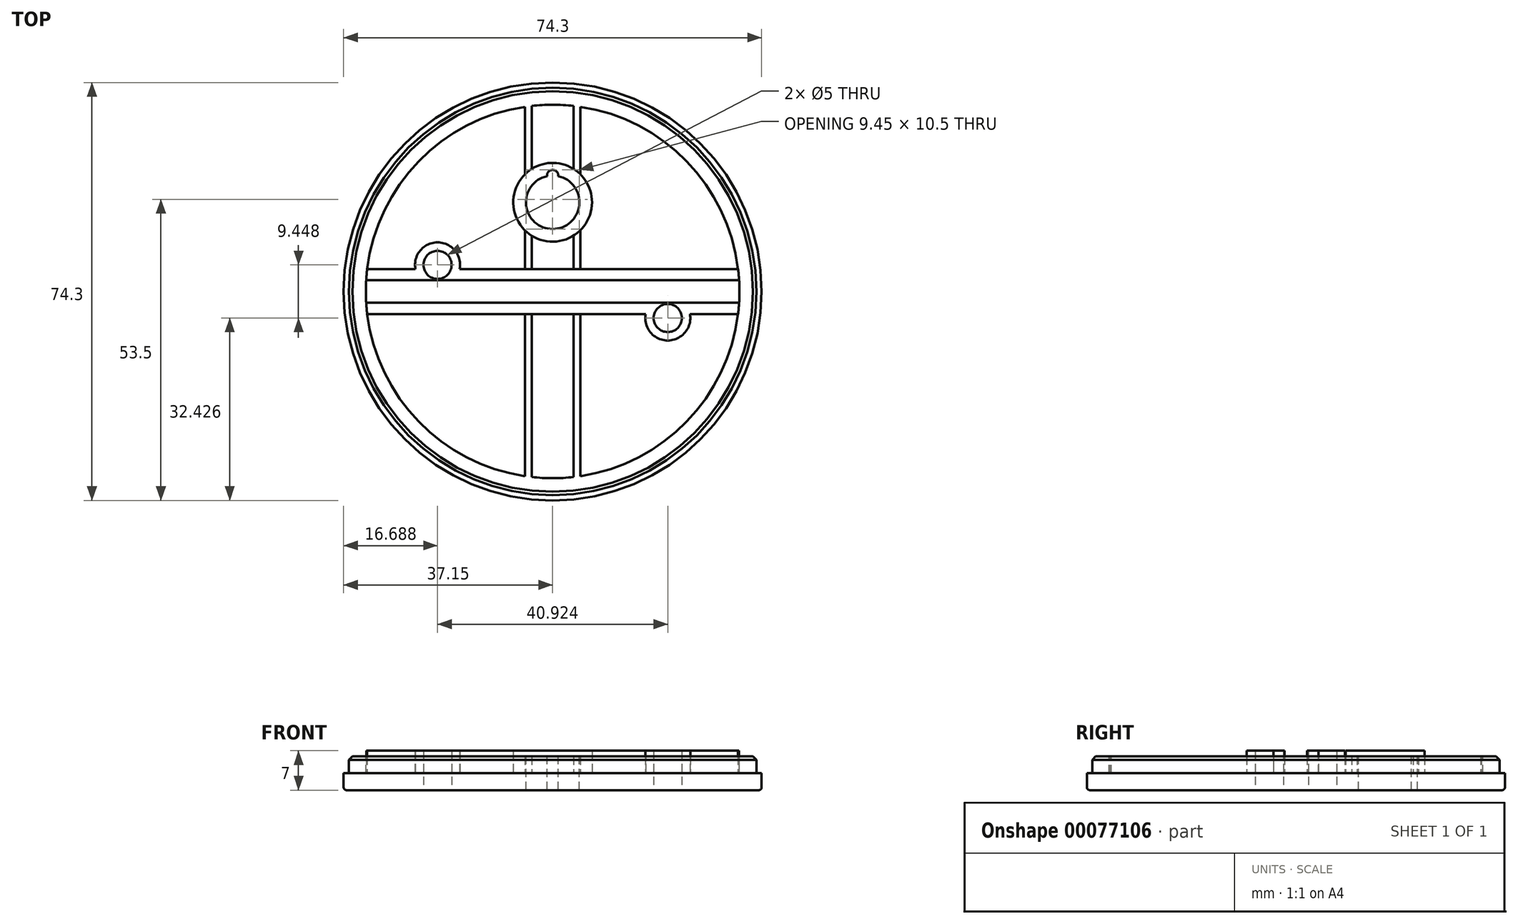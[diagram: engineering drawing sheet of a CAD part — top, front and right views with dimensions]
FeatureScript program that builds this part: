
annotation { "Feature Type Name" : "Feature", "Feature Type Description" : "" }
export const myFeature = defineFeature(function(context is Context, id is Id, definition is map)
    precondition{}
    {
        {
            var Q0;
            Q0=qCreatedBy(makeId("Front.planeOp"),FACE);
            var sketch = newSketch(context, id + "F0", { "sketchPlane" : qUnion([Q0])});
            skLineSegment(sketch, "E0.bottom", {"start": v(0, 0) * mm, "end": v(-33.2, 0) * mm});
            skLineSegment(sketch, "E0.top", {"start": v(0, -3) * mm, "end": v(-37.15, -3) * mm});
            skLineSegment(sketch, "E0.left", {"start": v(0, 0) * mm, "end": v(0, -3) * mm});
            skLineSegment(sketch, "E0.right", {"start": v(-37.15, 0) * mm, "end": v(-37.15, -3) * mm});
            skLineSegment(sketch, "E1.top", {"start": v(-36.2, 3) * mm, "end": v(-33.2, 3) * mm});
            skLineSegment(sketch, "E1.left", {"start": v(-36.2, 0) * mm, "end": v(-36.2, 3) * mm});
            skLineSegment(sketch, "E1.right", {"start": v(-33.2, 0) * mm, "end": v(-33.2, 3) * mm});
            skLineSegment(sketch, "E2.trimOffspring", {"start": v(-36.2, 0) * mm, "end": v(-37.15, 0) * mm});
            skLineSegment(sketch, "E3", {"start": v(0, 23.02) * mm, "end": v(0, -39) * mm, "construction": true});
            skSolve(sketch);
        }
        {
            var Q0;
            Q0=makeQuery(id+"F0.imprint","IMPRINT",FACE,{"disambiguationData":[TD([[makeQuery(id+"F0.imprint","IMPRINT",EDGE,{"derivedFrom":sQuery(id+"F0.wireOp",EDGE,"E0.bottom")}),1.0]])]});
            var Q1;
            Q1=sQuery(id+"F0.wireOp",EDGE,"E3");
            revolve(context, id + "F1", {"surfaceOperationType" : NewSurfaceOperationType.NEW, "entities" : qUnion([Q0]), "axis" : qUnion([Q1]), "revolveType" : RevolveType.FULL});
        }
        {
            var Q0;
            Q0=makeQuery(id+"F1.opRevolve","SWEPT_FACE",FACE,{"disambiguationData":[OSD([sQuery(id+"F0.wireOp",EDGE,"E0.bottom")])]});
            var sketch = newSketch(context, id + "F2", { "sketchPlane" : qUnion([Q0])});
            skLineSegment(sketch, "E4.bottom", {"start": v(-34.3, 2) * mm, "end": v(34, 2) * mm});
            skLineSegment(sketch, "E4.top", {"start": v(-34.3, 4) * mm, "end": v(34, 4) * mm});
            skLineSegment(sketch, "E4.left", {"start": v(-34.3, 2) * mm, "end": v(-34.3, 4) * mm});
            skLineSegment(sketch, "E4.right", {"start": v(34, 2) * mm, "end": v(34, 4) * mm});
            skLineSegment(sketch, "E5.MirrorCS", {"start": v(-34.3, -2) * mm, "end": v(34, -2) * mm});
            skLineSegment(sketch, "E6.MirrorCS", {"start": v(-34.3, -2) * mm, "end": v(-34.3, -4) * mm});
            skLineSegment(sketch, "E7.MirrorCS", {"start": v(-34.3, -4) * mm, "end": v(34, -4) * mm});
            skLineSegment(sketch, "E8.MirrorCS", {"start": v(34, -2) * mm, "end": v(34, -4) * mm});
            skSolve(sketch);
        }
        {
            var Q0;
            {var subQ0=sQuery(id+"F2.wireOp",EDGE,"E4.bottom");var subQ1=makeQuery(id+"F1.opRevolve","SWEPT_EDGE",EDGE,{"disambiguationData":[OSD([sQuery(id+"F0.wireOp",EDGE,"E0.bottom"),sQuery(id+"F0.wireOp",EDGE,"E1.right")])]});var subQ2=makeQuery(id+"F2.imprint","INTERSECT",VERTEX,{"disambiguationData":[OD(0.0)],"derivedFrom":[subQ1,subQ0]});Q0=makeQuery(id+"F2.imprint","IMPRINT",FACE,{"disambiguationData":[TD([[makeQuery(id+"F2.imprint","IMPRINT",EDGE,{"disambiguationData":[TD([[subQ2,-1.0]])],"derivedFrom":subQ0}),1.0]])]});}
            var Q1;
            {var subQ0=sQuery(id+"F2.wireOp",EDGE,"E5.MirrorCS");var subQ1=makeQuery(id+"F1.opRevolve","SWEPT_EDGE",EDGE,{"disambiguationData":[OSD([sQuery(id+"F0.wireOp",EDGE,"E0.bottom"),sQuery(id+"F0.wireOp",EDGE,"E1.right")])]});var subQ2=makeQuery(id+"F2.imprint","INTERSECT",VERTEX,{"disambiguationData":[OD(0.0)],"derivedFrom":[subQ1,subQ0]});Q1=makeQuery(id+"F2.imprint","IMPRINT",FACE,{"disambiguationData":[TD([[makeQuery(id+"F2.imprint","IMPRINT",EDGE,{"disambiguationData":[TD([[subQ2,-1.0]])],"derivedFrom":subQ0}),-1.0]])]});}
            extrude(context, id + "F3", {"entities" : qUnion([Q0, Q1]), "operationType" : NewBodyOperationType.ADD, "depth" : 4 * mm, "offsetDistance" : 25 * mm});
        }
        {
            var Q0;
            Q0=makeQuery(id+"F3.boolean.opBoolean","SPLIT",FACE,{"disambiguationData":[TD([makeQuery(id+"F3.opExtrude","SWEPT_FACE",FACE,{"disambiguationData":[OSD([sQuery(id+"F2.wireOp",EDGE,"E4.top")])]})])],"derivedFrom":makeQuery(id+"F1.opRevolve","SWEPT_FACE",FACE,{"disambiguationData":[OSD([sQuery(id+"F0.wireOp",EDGE,"E0.bottom")])]})});
            var sketch = newSketch(context, id + "F4", { "sketchPlane" : qUnion([Q0])});
            skCircle(sketch, "E9", {"center": v(0, 0) * mm, "radius": 25 * mm});
            skSolve(sketch);
        }
        {
            var Q0;
            {var subQ0=sQuery(id+"F4.wireOp",EDGE,"E9");var subQ1=sQuery(id+"F2.wireOp",EDGE,"E4.top");var subQ2=makeQuery(id+"F3.opExtrude","CAP_EDGE",EDGE,{"disambiguationData":[OSD([subQ1])],"isStart":true});var subQ3=makeQuery(id+"F4.imprint","INTERSECT",VERTEX,{"disambiguationData":[OD(0.0)],"derivedFrom":[subQ2,subQ0]});Q0=makeQuery(id+"F4.imprint","IMPRINT",FACE,{"disambiguationData":[TD([[makeQuery(id+"F4.imprint","IMPRINT",EDGE,{"disambiguationData":[TD([[subQ3,1.0]])],"derivedFrom":subQ0}),-1.0]])]});}
            var sketch = newSketch(context, id + "F5", { "sketchPlane" : qUnion([Q0])});
            skLineSegment(sketch, "E10", {"start": v(-33.33, 7.7) * mm, "end": v(0, 0) * mm, "construction": true});
            skLineSegment(sketch, "E11", {"start": v(0, 0) * mm, "end": v(33.42, -7.72) * mm, "construction": true});
            skLineSegment(sketch, "E12.bottom", {"start": v(-4.93, 3.16) * mm, "end": v(-3.73, 3.16) * mm});
            skLineSegment(sketch, "E12.top", {"start": v(-4.93, 33.8) * mm, "end": v(-3.73, 33.8) * mm});
            skLineSegment(sketch, "E12.left", {"start": v(-4.93, 3.16) * mm, "end": v(-4.93, 33.8) * mm});
            skLineSegment(sketch, "E12.right", {"start": v(-3.73, 3.16) * mm, "end": v(-3.73, 33.8) * mm});
            skLineSegment(sketch, "E13.MirrorCS", {"start": v(3.73, 3.16) * mm, "end": v(3.73, 33.8) * mm});
            skLineSegment(sketch, "E14.MirrorCS", {"start": v(4.93, 3.16) * mm, "end": v(4.93, 33.8) * mm});
            skLineSegment(sketch, "E15.MirrorCS", {"start": v(4.93, 33.8) * mm, "end": v(3.73, 33.8) * mm});
            skLineSegment(sketch, "E16.MirrorCS", {"start": v(4.93, 3.16) * mm, "end": v(3.73, 3.16) * mm});
            skLineSegment(sketch, "E17.MirrorCS", {"start": v(-4.93, -33.8) * mm, "end": v(-3.73, -33.8) * mm});
            skLineSegment(sketch, "E18.MirrorCS", {"start": v(-3.73, -3.16) * mm, "end": v(-3.73, -33.8) * mm});
            skLineSegment(sketch, "E19.MirrorCS", {"start": v(-4.93, -3.16) * mm, "end": v(-3.73, -3.16) * mm});
            skLineSegment(sketch, "E20.MirrorCS", {"start": v(-4.93, -3.16) * mm, "end": v(-4.93, -33.8) * mm});
            skLineSegment(sketch, "E21.MirrorCS", {"start": v(4.93, -3.16) * mm, "end": v(3.73, -3.16) * mm});
            skLineSegment(sketch, "E22.MirrorCS", {"start": v(4.93, -33.8) * mm, "end": v(3.73, -33.8) * mm});
            skLineSegment(sketch, "E23.MirrorCS", {"start": v(3.73, -3.16) * mm, "end": v(3.73, -33.8) * mm});
            skLineSegment(sketch, "E24.MirrorCS", {"start": v(4.93, -3.16) * mm, "end": v(4.93, -33.8) * mm});
            skCircle(sketch, "E25", {"center": v(0, 0) * mm, "radius": 21 * mm, "construction": true});
            skCircle(sketch, "E26", {"center": v(-20.46, 4.72) * mm, "radius": 2.5 * mm});
            skCircle(sketch, "E27", {"center": v(20.46, -4.72) * mm, "radius": 2.5 * mm});
            skArc(sketch, "E28", {"start": v(-17.49, 2.05) * mm, "mid": v(-20.46, 8.72) * mm, "end": v(-23.44, 2.05) * mm});
            skArc(sketch, "E29", {"start": v(17.54, -2) * mm, "mid": v(20.46, -8.72) * mm, "end": v(23.38, -2) * mm});
            skLineSegment(sketch, "E30", {"start": v(-23.44, 2.05) * mm, "end": v(-17.49, 2.05) * mm});
            skLineSegment(sketch, "E31", {"start": v(17.54, -2) * mm, "end": v(23.38, -2) * mm});
            skSolve(sketch);
        }
        {
            var Q0;
            Q0=makeQuery(id+"F5.imprint","IMPRINT",FACE,{"disambiguationData":[TD([[makeQuery(id+"F5.imprint","IMPRINT",EDGE,{"derivedFrom":sQuery(id+"F5.wireOp",EDGE,"E17.MirrorCS")}),1.0]])]});
            var Q1;
            Q1=makeQuery(id+"F5.imprint","IMPRINT",FACE,{"disambiguationData":[TD([[makeQuery(id+"F5.imprint","IMPRINT",EDGE,{"derivedFrom":sQuery(id+"F5.wireOp",EDGE,"E21.MirrorCS")}),1.0]])]});
            var Q2;
            {var subQ0=sQuery(id+"F5.wireOp",EDGE,"E12.bottom");Q2=makeQuery(id+"F5.imprint","IMPRINT",FACE,{"disambiguationData":[TD([[makeQuery(id+"F5.imprint","IMPRINT",EDGE,{"derivedFrom":subQ0}),1.0]])]});}
            var Q3;
            {var subQ0=sQuery(id+"F5.wireOp",EDGE,"E16.MirrorCS");Q3=makeQuery(id+"F5.imprint","IMPRINT",FACE,{"disambiguationData":[TD([[makeQuery(id+"F5.imprint","IMPRINT",EDGE,{"derivedFrom":subQ0}),-1.0]])]});}
            var Q4;
            {var subQ0=sQuery(id+"F5.wireOp",EDGE,"E13.MirrorCS");var subQ1=sQuery(id+"F4.wireOp",EDGE,"E9");var subQ2=sQuery(id+"F2.wireOp",EDGE,"E4.top");var subQ3=makeQuery(id+"F3.opExtrude","CAP_EDGE",EDGE,{"disambiguationData":[OSD([subQ2])],"isStart":true});var subQ4=makeQuery(id+"F4.imprint","IMPRINT",EDGE,{"disambiguationData":[TD([[makeQuery(id+"F4.imprint","INTERSECT",VERTEX,{"disambiguationData":[OD(0.0)],"derivedFrom":[subQ3,subQ1]}),1.0]])],"derivedFrom":subQ1});var subQ5=makeQuery(id+"F5.imprint","INTERSECT",VERTEX,{"derivedFrom":[subQ4,subQ0]});Q4=makeQuery(id+"F5.imprint","IMPRINT",FACE,{"disambiguationData":[TD([[makeQuery(id+"F5.imprint","IMPRINT",EDGE,{"disambiguationData":[TD([[subQ5,-1.0]])],"derivedFrom":subQ0}),-1.0]])]});}
            var Q5;
            {var subQ0=sQuery(id+"F5.wireOp",EDGE,"E12.left");var subQ1=sQuery(id+"F4.wireOp",EDGE,"E9");var subQ2=sQuery(id+"F2.wireOp",EDGE,"E4.top");var subQ3=makeQuery(id+"F3.opExtrude","CAP_EDGE",EDGE,{"disambiguationData":[OSD([subQ2])],"isStart":true});var subQ4=makeQuery(id+"F4.imprint","IMPRINT",EDGE,{"disambiguationData":[TD([[makeQuery(id+"F4.imprint","INTERSECT",VERTEX,{"disambiguationData":[OD(0.0)],"derivedFrom":[subQ3,subQ1]}),1.0]])],"derivedFrom":subQ1});var subQ5=makeQuery(id+"F5.imprint","INTERSECT",VERTEX,{"derivedFrom":[subQ4,subQ0]});Q5=makeQuery(id+"F5.imprint","IMPRINT",FACE,{"disambiguationData":[TD([[makeQuery(id+"F5.imprint","IMPRINT",EDGE,{"disambiguationData":[TD([[subQ5,-1.0]])],"derivedFrom":subQ0}),-1.0]])]});}
            extrude(context, id + "F6", {"entities" : qUnion([Q0, Q1, Q2, Q3, Q4, Q5]), "operationType" : NewBodyOperationType.ADD, "depth" : 3 * mm, "offsetDistance" : 25 * mm});
        }
        {
            var Q0;
            Q0=makeQuery(id+"F5.imprint","IMPRINT",FACE,{"disambiguationData":[TD([[makeQuery(id+"F5.imprint","IMPRINT",EDGE,{"derivedFrom":sQuery(id+"F5.wireOp",EDGE,"E27")}),-1.0]])]});
            var Q1;
            Q1=makeQuery(id+"F5.imprint","IMPRINT",FACE,{"disambiguationData":[TD([[makeQuery(id+"F5.imprint","IMPRINT",EDGE,{"derivedFrom":sQuery(id+"F5.wireOp",EDGE,"E26")}),-1.0]])]});
            extrude(context, id + "F7", {"entities" : qUnion([Q0, Q1]), "operationType" : NewBodyOperationType.ADD, "depth" : 4 * mm, "offsetDistance" : 25 * mm});
        }
        {
            var Q0;
            {var subQ0=sQuery(id+"F5.wireOp",EDGE,"E26");var subQ1=sQuery(id+"F4.wireOp",EDGE,"E9");var subQ2=makeQuery(id+"F3.opExtrude","CAP_EDGE",EDGE,{"disambiguationData":[OSD([sQuery(id+"F2.wireOp",EDGE,"E4.top")])],"isStart":true});var subQ3=makeQuery(id+"F4.imprint","IMPRINT",EDGE,{"disambiguationData":[TD([[makeQuery(id+"F4.imprint","INTERSECT",VERTEX,{"disambiguationData":[OD(0.0)],"derivedFrom":[subQ2,subQ1]}),1.0]])],"derivedFrom":subQ1});var subQ4=makeQuery(id+"F5.imprint","INTERSECT",VERTEX,{"disambiguationData":[OD(0.0)],"derivedFrom":[subQ3,subQ0]});Q0=makeQuery(id+"F5.imprint","IMPRINT",FACE,{"disambiguationData":[TD([[makeQuery(id+"F5.imprint","IMPRINT",EDGE,{"disambiguationData":[TD([[subQ4,-1.0]])],"derivedFrom":subQ0}),1.0]])]});}
            var Q1;
            {var subQ0=sQuery(id+"F5.wireOp",EDGE,"E26");var subQ1=sQuery(id+"F4.wireOp",EDGE,"E9");var subQ2=makeQuery(id+"F3.opExtrude","CAP_EDGE",EDGE,{"disambiguationData":[OSD([sQuery(id+"F2.wireOp",EDGE,"E4.top")])],"isStart":true});var subQ3=makeQuery(id+"F4.imprint","IMPRINT",EDGE,{"disambiguationData":[TD([[makeQuery(id+"F4.imprint","INTERSECT",VERTEX,{"disambiguationData":[OD(0.0)],"derivedFrom":[subQ2,subQ1]}),1.0]])],"derivedFrom":subQ1});var subQ4=makeQuery(id+"F5.imprint","INTERSECT",VERTEX,{"disambiguationData":[OD(0.0)],"derivedFrom":[subQ3,subQ0]});Q1=makeQuery(id+"F5.imprint","IMPRINT",FACE,{"disambiguationData":[TD([[makeQuery(id+"F5.imprint","IMPRINT",EDGE,{"disambiguationData":[TD([[subQ4,1.0]])],"derivedFrom":subQ0}),1.0]])]});}
            var Q2;
            Q2=makeQuery(id+"F5.imprint","IMPRINT",FACE,{"disambiguationData":[TD([[makeQuery(id+"F5.imprint","IMPRINT",EDGE,{"derivedFrom":sQuery(id+"F5.wireOp",EDGE,"E27")}),1.0]])]});
            extrude(context, id + "F8", {"entities" : qUnion([Q0, Q1, Q2]), "operationType" : NewBodyOperationType.REMOVE, "oppositeDirection" : true, "depth" : 25 * mm, "offsetDistance" : 25 * mm, "symmetric" : true});
        }
        {
            var Q0;
            {var subQ0=sQuery(id+"F4.wireOp",EDGE,"E9");var subQ1=makeQuery(id+"F3.opExtrude","CAP_EDGE",EDGE,{"disambiguationData":[OSD([sQuery(id+"F2.wireOp",EDGE,"E4.top")])],"isStart":true});var subQ2=makeQuery(id+"F4.imprint","INTERSECT",VERTEX,{"disambiguationData":[OD(0.0)],"derivedFrom":[subQ1,subQ0]});Q0=makeQuery(id+"F4.imprint","IMPRINT",FACE,{"disambiguationData":[TD([[makeQuery(id+"F4.imprint","IMPRINT",EDGE,{"disambiguationData":[TD([[subQ2,1.0]])],"derivedFrom":subQ0}),1.0]])]});}
            var sketch = newSketch(context, id + "F9", { "sketchPlane" : qUnion([Q0])});
            skCircle(sketch, "E32", {"center": v(0, 15.85) * mm, "radius": 4.75 * mm});
            skCircle(sketch, "E33", {"center": v(0, 15.85) * mm, "radius": 7 * mm});
            skCircle(sketch, "E34", {"center": v(0, 20.6) * mm, "radius": 1 * mm});
            skSolve(sketch);
        }
        {
            var Q0;
            {var subQ0=sQuery(id+"F9.wireOp",EDGE,"E34");var subQ1=sQuery(id+"F9.wireOp",EDGE,"E32");var subQ2=makeQuery(id+"F9.imprint","INTERSECT",VERTEX,{"disambiguationData":[OD(0.0)],"derivedFrom":[subQ1,subQ0]});Q0=makeQuery(id+"F9.imprint","IMPRINT",FACE,{"disambiguationData":[TD([[makeQuery(id+"F9.imprint","IMPRINT",EDGE,{"disambiguationData":[TD([[subQ2,1.0]])],"derivedFrom":subQ1}),-1.0]])]});}
            var Q1;
            {var subQ0=sQuery(id+"F9.wireOp",EDGE,"E34");var subQ1=sQuery(id+"F9.wireOp",EDGE,"E32");var subQ2=makeQuery(id+"F9.imprint","INTERSECT",VERTEX,{"disambiguationData":[OD(0.0)],"derivedFrom":[subQ1,subQ0]});Q1=makeQuery(id+"F9.imprint","IMPRINT",FACE,{"disambiguationData":[TD([[makeQuery(id+"F9.imprint","IMPRINT",EDGE,{"disambiguationData":[TD([[subQ2,1.0]])],"derivedFrom":subQ1}),1.0]])]});}
            var Q2;
            {var subQ0=sQuery(id+"F9.wireOp",EDGE,"E34");var subQ1=sQuery(id+"F9.wireOp",EDGE,"E32");var subQ2=makeQuery(id+"F9.imprint","INTERSECT",VERTEX,{"disambiguationData":[OD(0.0)],"derivedFrom":[subQ1,subQ0]});Q2=makeQuery(id+"F9.imprint","IMPRINT",FACE,{"disambiguationData":[TD([[makeQuery(id+"F9.imprint","IMPRINT",EDGE,{"disambiguationData":[TD([[subQ2,-1.0]])],"derivedFrom":subQ1}),1.0]])]});}
            extrude(context, id + "F10", {"entities" : qUnion([Q0, Q1, Q2]), "operationType" : NewBodyOperationType.REMOVE, "oppositeDirection" : true, "depth" : 25 * mm, "offsetDistance" : 25 * mm, "symmetric" : true});
        }
        {
            var Q0;
            Q0=makeQuery(id+"F9.imprint","IMPRINT",FACE,{"disambiguationData":[TD([[makeQuery(id+"F9.imprint","IMPRINT",EDGE,{"derivedFrom":sQuery(id+"F9.wireOp",EDGE,"E33")}),1.0]])]});
            extrude(context, id + "F11", {"entities" : qUnion([Q0]), "operationType" : NewBodyOperationType.ADD, "depth" : 4 * mm, "offsetDistance" : 25 * mm});
        }
        {
            var Q0;
            Q0=makeQuery(id+"F1.opRevolve","SWEPT_EDGE",EDGE,{"disambiguationData":[OSD([sQuery(id+"F0.wireOp",EDGE,"E1.top"),sQuery(id+"F0.wireOp",EDGE,"E1.left")])]});
            chamfer(context, id + "F12", {"entities" : qUnion([Q0]), "width" : .6 * mm, "tangentPropagation" : true});
        }
        {
            var Q0;
            Q0=makeQuery(id+"F1.opRevolve","SWEPT_EDGE",EDGE,{"disambiguationData":[OSD([sQuery(id+"F0.wireOp",EDGE,"E0.top"),sQuery(id+"F0.wireOp",EDGE,"E0.right")])]});
            fillet(context, id + "F13", {"entities" : qUnion([Q0]), "radius" : .5 * mm, "tangentPropagation" : true, "allowEdgeOverflow" : false});
        }
    });
